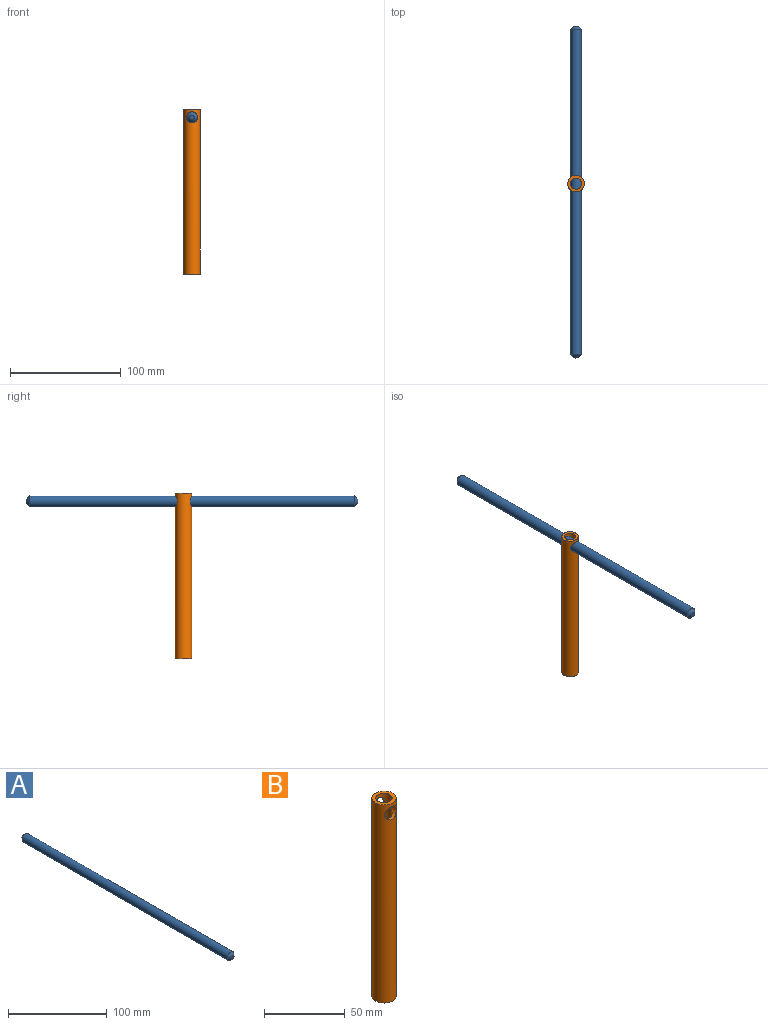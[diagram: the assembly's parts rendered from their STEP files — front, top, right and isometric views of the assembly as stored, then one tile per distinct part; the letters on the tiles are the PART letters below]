
ASSEMBLY  parts=2 mates=1
PART A: 5 faces, bbox 10x300x10 mm
  f0: cylinder r=5mm len=294mm, axis (0,1,0), area 9236.3mm2, adj f3,f4
  f1: plane 4x4mm, normal (0,-1,0), area 12.6mm2, adj f4
  f2: plane 4x4mm, normal (0,1,0), area 12.6mm2, adj f3
  f3: cone r=5mm half-angle=45deg, axis (0,-1,0), area 93.3mm2, adj f0,f2
  f4: cone r=2mm half-angle=45deg, axis (0,1,0), area 93.3mm2, adj f0,f1
PART B: 9 faces, bbox 15x15x150 mm
  f0: cylinder r=5mm len=142.5mm, axis (0,0,-1), area 4359.4mm2, adj f4,f5,f6,f7,f8
  f1: cylinder r=7.5mm len=150mm, axis (0,0,-1), area 6883.5mm2, adj f3,f4,f5,f6,f7,f8
  f2: cylinder r=5mm len=10mm, axis (0,0,-1), area 135.6mm2, adj f3,f5,f6
  f3: plane 15x15mm, normal (0,0,1), area 98.2mm2, adj f1,f2
  f4: plane 15x15mm, normal (0,0,-1), area 98.2mm2, adj f0,f1
  f5: cylinder r=5mm len=10mm, axis (0,-1,0), area 106.8mm2, adj f0,f1,f2
  f6: cylinder r=5mm len=10mm, axis (0,-1,0), area 106.7mm2, adj f0,f1,f2
  f7: cylinder r=1.65mm len=3.3mm, axis (-1,0,0), area 26.4mm2, adj f0,f1
  f8: cylinder r=1.65mm len=3.3mm, axis (-1,0,0), area 26.4mm2, adj f0,f1
PLACE A t=(-63.39,58.84,-3)mm
PLACE B t=(-63.39,-83.6,-145.5)mm
MATE slider A.f0 <-> B.f5  axis (0,1,0) through (-63.39,-91.16,-3)mm
